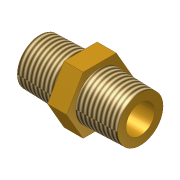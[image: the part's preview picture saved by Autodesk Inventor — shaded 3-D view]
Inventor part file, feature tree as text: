
AUTODESK INVENTOR PART (.ipt)
format: ipt  version: 2014 SP1 (Build 180222100, 222)  size: 108,032 bytes
history: native  units: mm (DEFAULTED — no unit token found)
features: thread x4, sketch x1, imported_body x1
ambient origin geometry x8: Origin, YZ Plane, XZ Plane, XY Plane, X Axis, Y Axis, Z Axis, Center Point
bodies: Solid1 (feature_tree)
feature tree (6):
  sketch  "Sketch1"
  imported_body  "Base1"
  thread  "Thread1"  [1 undecoded]
  thread  "Thread2"  [1 undecoded]
  thread  "Thread3"  [1 undecoded]
  thread  "Thread4"  [1 undecoded]
note: 4 required parameter values undecoded (feature->parameter linkage not recoverable at this tier; creation-order binding heuristic only, values carry confidence <= 0.55)
